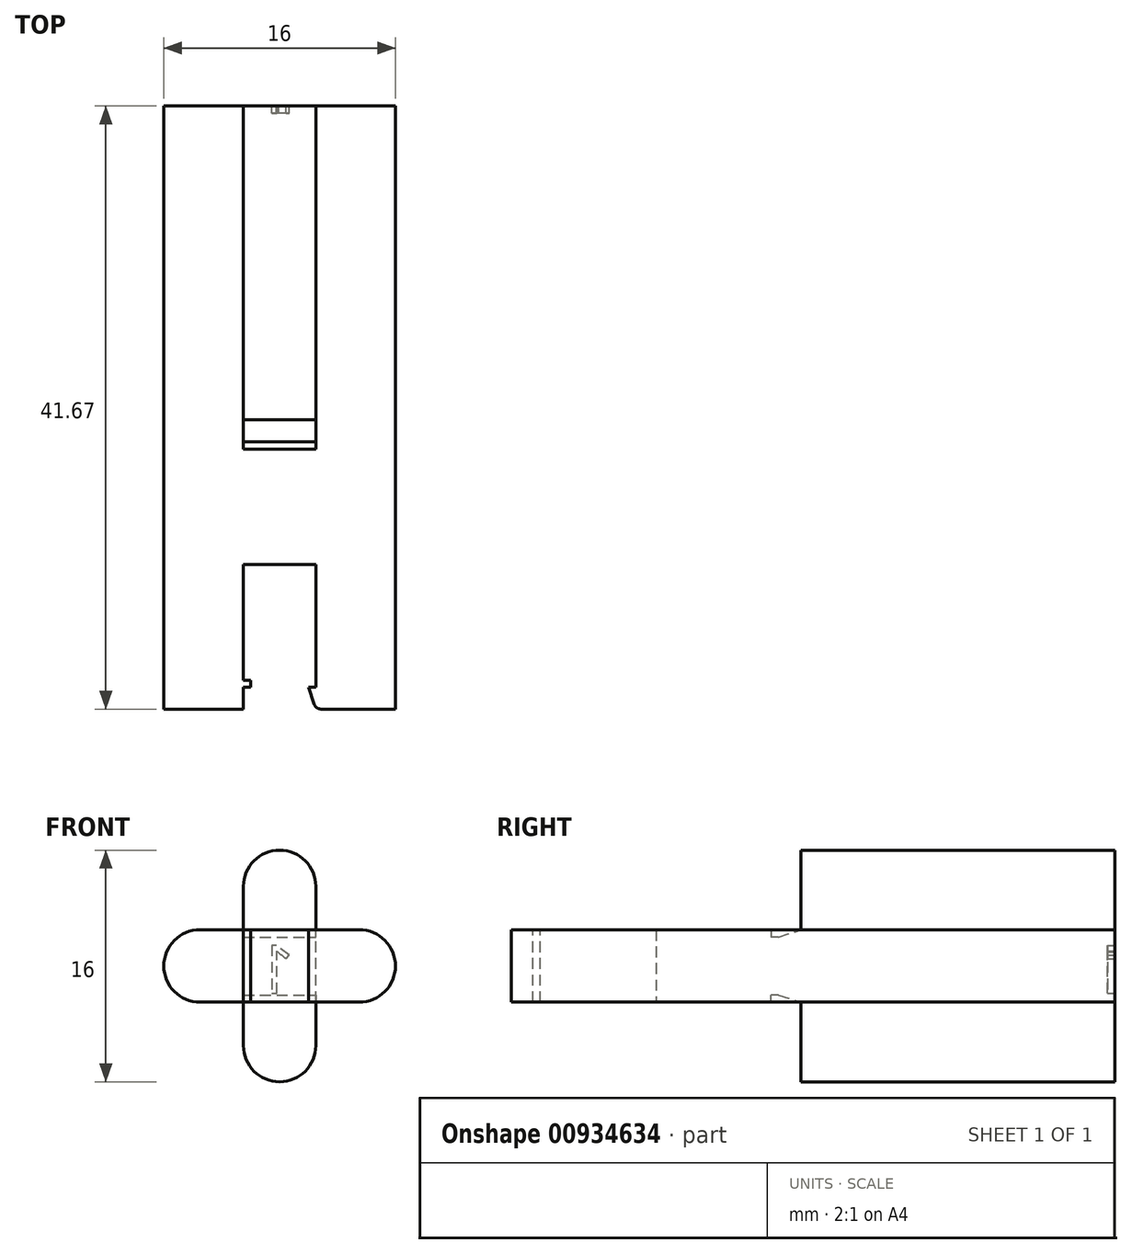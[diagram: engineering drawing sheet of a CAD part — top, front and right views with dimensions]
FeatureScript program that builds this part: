
annotation { "Feature Type Name" : "Feature", "Feature Type Description" : "" }
export const myFeature = defineFeature(function(context is Context, id is Id, definition is map)
    precondition{}
    {
        {
            var Q0;
            Q0=qCreatedBy(makeId("Front.planeOp"),FACE);
            var sketch = newSketch(context, id + "F0", { "sketchPlane" : qUnion([Q0])});
            skLineSegment(sketch, "E0.bottom", {"start": v(2.5, 8) * mm, "end": v(-2.5, 8) * mm});
            skLineSegment(sketch, "E0.top", {"start": v(2.5, -8) * mm, "end": v(-2.5, -8) * mm});
            skLineSegment(sketch, "E0.left", {"start": v(2.5, 8) * mm, "end": v(2.5, -8) * mm});
            skLineSegment(sketch, "E0.right", {"start": v(-2.5, 8) * mm, "end": v(-2.5, -8) * mm});
            skPoint(sketch, "E0.middle", {"position": v(0, 0) * mm});
            skLineSegment(sketch, "E1.bottom", {"start": v(-8, -2.5) * mm, "end": v(8, -2.5) * mm});
            skLineSegment(sketch, "E1.top", {"start": v(-8, 2.5) * mm, "end": v(8, 2.5) * mm});
            skLineSegment(sketch, "E1.left", {"start": v(-8, -2.5) * mm, "end": v(-8, 2.5) * mm});
            skLineSegment(sketch, "E1.right", {"start": v(8, -2.5) * mm, "end": v(8, 2.5) * mm});
            skSolve(sketch);
        }
        {
            var Q0;
            {var subQ5=sQuery(id+"F0.wireOp",EDGE,"E1.left");Q0=makeQuery(id+"F0.imprint","IMPRINT",FACE,{"disambiguationData":[TD([[makeQuery(id+"F0.imprint","IMPRINT",EDGE,{"derivedFrom":subQ5}),-1.0]])]});}
            var Q1;
            {var subQ0=sQuery(id+"F0.wireOp",EDGE,"E1.top");var subQ1=sQuery(id+"F0.wireOp",EDGE,"E0.left");var subQ2=makeQuery(id+"F0.imprint","INTERSECT",VERTEX,{"derivedFrom":[subQ1,subQ0]});Q1=makeQuery(id+"F0.imprint","IMPRINT",FACE,{"disambiguationData":[TD([[makeQuery(id+"F0.imprint","IMPRINT",EDGE,{"disambiguationData":[TD([[subQ2,-1.0]])],"derivedFrom":subQ1}),-1.0]])]});}
            var Q2;
            {var subQ5=sQuery(id+"F0.wireOp",EDGE,"E1.right");Q2=makeQuery(id+"F0.imprint","IMPRINT",FACE,{"disambiguationData":[TD([[makeQuery(id+"F0.imprint","IMPRINT",EDGE,{"derivedFrom":subQ5}),1.0]])]});}
            var Q3;
            {var subQ0=sQuery(id+"F0.wireOp",EDGE,"E0.top");Q3=makeQuery(id+"F0.imprint","IMPRINT",FACE,{"disambiguationData":[TD([[makeQuery(id+"F0.imprint","IMPRINT",EDGE,{"derivedFrom":subQ0}),-1.0]])]});}
            var Q4;
            {var subQ0=sQuery(id+"F0.wireOp",EDGE,"E0.bottom");Q4=makeQuery(id+"F0.imprint","IMPRINT",FACE,{"disambiguationData":[TD([[makeQuery(id+"F0.imprint","IMPRINT",EDGE,{"derivedFrom":subQ0}),1.0]])]});}
            extrude(context, id + "F1", {"entities" : qUnion([Q0, Q1, Q2, Q3, Q4]), "depth" : 233.86 * mm, "offsetDistance" : 25.4 * mm});
        }
        {
            var Q0;
            Q0=makeQuery(id+"F1.opExtrude","SWEPT_EDGE",EDGE,{"disambiguationData":[OSD([sQuery(id+"F0.wireOp",EDGE,"E0.bottom"),sQuery(id+"F0.wireOp",EDGE,"E0.right")])]});
            var Q1;
            Q1=makeQuery(id+"F1.opExtrude","SWEPT_EDGE",EDGE,{"disambiguationData":[OSD([sQuery(id+"F0.wireOp",EDGE,"E0.bottom"),sQuery(id+"F0.wireOp",EDGE,"E0.left")])]});
            var Q2;
            Q2=makeQuery(id+"F1.opExtrude","SWEPT_EDGE",EDGE,{"disambiguationData":[OSD([sQuery(id+"F0.wireOp",EDGE,"E1.top"),sQuery(id+"F0.wireOp",EDGE,"E1.left")])]});
            var Q3;
            Q3=makeQuery(id+"F1.opExtrude","SWEPT_EDGE",EDGE,{"disambiguationData":[OSD([sQuery(id+"F0.wireOp",EDGE,"E1.bottom"),sQuery(id+"F0.wireOp",EDGE,"E1.left")])]});
            var Q4;
            Q4=makeQuery(id+"F1.opExtrude","SWEPT_EDGE",EDGE,{"disambiguationData":[OSD([sQuery(id+"F0.wireOp",EDGE,"E0.top"),sQuery(id+"F0.wireOp",EDGE,"E0.right")])]});
            var Q5;
            Q5=makeQuery(id+"F1.opExtrude","SWEPT_EDGE",EDGE,{"disambiguationData":[OSD([sQuery(id+"F0.wireOp",EDGE,"E0.top"),sQuery(id+"F0.wireOp",EDGE,"E0.left")])]});
            var Q6;
            Q6=makeQuery(id+"F1.opExtrude","SWEPT_EDGE",EDGE,{"disambiguationData":[OSD([sQuery(id+"F0.wireOp",EDGE,"E1.bottom"),sQuery(id+"F0.wireOp",EDGE,"E1.right")])]});
            var Q7;
            Q7=makeQuery(id+"F1.opExtrude","SWEPT_EDGE",EDGE,{"disambiguationData":[OSD([sQuery(id+"F0.wireOp",EDGE,"E1.top"),sQuery(id+"F0.wireOp",EDGE,"E1.right")])]});
            fillet(context, id + "F2", {"entities" : qUnion([Q0, Q1, Q2, Q3, Q4, Q5, Q6, Q7]), "radius" : 2.5 * mm, "tangentPropagation" : true, "allowEdgeOverflow" : false});
        }
        {
            var Q0;
            Q0=qCreatedBy(makeId("Front.planeOp"),FACE);
            var sketch = newSketch(context, id + "F3", { "sketchPlane" : qUnion([Q0])});
            skCircle(sketch, "E2", {"center": v(0, 0) * mm, "radius": 14.75 * mm});
            skCircle(sketch, "E3", {"center": v(0, 0) * mm, "radius": 12.2 * mm});
            skSolve(sketch);
        }
        {
            var Q0;
            Q0=makeQuery(id+"F3.imprint","IMPRINT",FACE,{"disambiguationData":[TD([[makeQuery(id+"F3.imprint","IMPRINT",EDGE,{"derivedFrom":sQuery(id+"F3.wireOp",EDGE,"E2")}),1.0]])]});
            var Q1;
            Q1=makeQuery(id+"F3.imprint","IMPRINT",FACE,{"disambiguationData":[TD([[makeQuery(id+"F3.imprint","IMPRINT",EDGE,{"derivedFrom":sQuery(id+"F3.wireOp",EDGE,"E3")}),1.0]])]});
            extrude(context, id + "F4", {"entities" : qUnion([Q0, Q1]), "operationType" : NewBodyOperationType.ADD, "oppositeDirection" : true, "depth" : 13.8 * mm, "offsetDistance" : 25.4 * mm});
        }
        {
            var Q0;
            {var subQ0=sQuery(id+"F0.wireOp",EDGE,"E0.right");Q0=makeQuery(id+"F1.opExtrude","CAP_EDGE",EDGE,{"disambiguationData":[OSD([subQ0]),TDD([makeQuery(id+"F0.imprint","IMPRINT",EDGE,{"disambiguationData":[TD([[makeQuery(id+"F0.imprint","INTERSECT",VERTEX,{"derivedFrom":[sQuery(id+"F0.wireOp",EDGE,"E0.bottom"),subQ0]}),-1.0]])],"derivedFrom":subQ0})])],"isStart":true});}
            var Q1;
            Q1=makeQuery(id+"F4.opExtrude","CAP_FACE",FACE,{"disambiguationData":[OSD([sQuery(id+"F3.wireOp",EDGE,"E2")])],"isStart":true});
            var Q2;
            Q2=makeQuery(id+"F4.opExtrude","CAP_EDGE",EDGE,{"disambiguationData":[OSD([sQuery(id+"F3.wireOp",EDGE,"E2")])],"isStart":false});
            fillet(context, id + "F5", {"entities" : qUnion([Q0, Q1, Q2]), "radius" : 0.5 * mm, "tangentPropagation" : true, "allowEdgeOverflow" : false});
        }
        {
            var Q0;
            Q0=qCreatedBy(makeId("Right.planeOp"),FACE);
            var sketch = newSketch(context, id + "F6", { "sketchPlane" : qUnion([Q0])});
            skLineSegment(sketch, "E4.bottom", {"start": v(5, 22.2) * mm, "end": v(8.8, 22.2) * mm});
            skLineSegment(sketch, "E4.top", {"start": v(5, 12.2) * mm, "end": v(8.8, 12.2) * mm});
            skLineSegment(sketch, "E4.left", {"start": v(5, 22.2) * mm, "end": v(5, 12.2) * mm});
            skLineSegment(sketch, "E4.right", {"start": v(8.8, 22.2) * mm, "end": v(8.8, 12.2) * mm});
            skLineSegment(sketch, "E5", {"start": v(0, 0) * mm, "end": v(33.95, 0) * mm});
            skSolve(sketch);
        }
        {
            var Q0;
            Q0=makeQuery(id+"F6.imprint","IMPRINT",FACE,{"disambiguationData":[TD([[makeQuery(id+"F6.imprint","IMPRINT",EDGE,{"derivedFrom":sQuery(id+"F6.wireOp",EDGE,"E4.bottom")}),-1.0]])]});
            var Q1;
            Q1=sQuery(id+"F6.wireOp",EDGE,"E5");
            revolve(context, id + "F7", {"operationType" : NewBodyOperationType.REMOVE, "surfaceOperationType" : NewSurfaceOperationType.NEW, "entities" : qUnion([Q0]), "axis" : qUnion([Q1]), "revolveType" : RevolveType.FULL, "oppositeDirection" : true});
        }
        {
            var Q0;
            Q0=makeQuery(id+"F1.opExtrude","CAP_FACE",FACE,{"disambiguationData":[OSD([sQuery(id+"F0.wireOp",EDGE,"E0.bottom"),sQuery(id+"F0.wireOp",EDGE,"E0.top"),sQuery(id+"F0.wireOp",EDGE,"E0.left"),sQuery(id+"F0.wireOp",EDGE,"E0.right"),sQuery(id+"F0.wireOp",EDGE,"E1.bottom"),sQuery(id+"F0.wireOp",EDGE,"E1.top"),sQuery(id+"F0.wireOp",EDGE,"E1.left"),sQuery(id+"F0.wireOp",EDGE,"E1.right")])],"isStart":false});
            var sketch = newSketch(context, id + "F8", { "sketchPlane" : qUnion([Q0])});
            skLineSegment(sketch, "E6.bottom", {"start": v(2.5, 10) * mm, "end": v(-2.5, 10) * mm});
            skLineSegment(sketch, "E6.top", {"start": v(2.5, -10) * mm, "end": v(-2.5, -10) * mm});
            skLineSegment(sketch, "E6.left", {"start": v(2.5, 10) * mm, "end": v(2.5, -10) * mm});
            skLineSegment(sketch, "E6.right", {"start": v(-2.5, 10) * mm, "end": v(-2.5, -10) * mm});
            skPoint(sketch, "E6.middle", {"position": v(0, 0) * mm});
            skSolve(sketch);
        }
        {
            var Q0;
            {var subQ1=sQuery(id+"F0.wireOp",EDGE,"E1.top");var subQ2=sQuery(id+"F0.wireOp",EDGE,"E1.bottom");var subQ3=sQuery(id+"F0.wireOp",EDGE,"E0.right");var subQ4=sQuery(id+"F0.wireOp",EDGE,"E0.left");var subQ5=sQuery(id+"F0.wireOp",EDGE,"E0.top");var subQ6=sQuery(id+"F0.wireOp",EDGE,"E0.bottom");var subQ7=makeQuery(id+"F1.opExtrude","CAP_FACE",FACE,{"disambiguationData":[OSD([subQ6,subQ5,subQ4,subQ3,subQ2,subQ1,sQuery(id+"F0.wireOp",EDGE,"E1.left"),sQuery(id+"F0.wireOp",EDGE,"E1.right")])],"isStart":false});var subQ11=makeQuery(id+"F2.opFillet","BLEND_EDGE",EDGE,{"blendedFrom":[makeQuery(id+"F1.opExtrude","SWEPT_EDGE",EDGE,{"disambiguationData":[OSD([subQ6,subQ4])]}),subQ7],"blendedInto":[subQ7]});Q0=makeQuery(id+"F8.imprint","IMPRINT",FACE,{"disambiguationData":[TD([[makeQuery(id+"F8.imprint","IMPRINT",EDGE,{"derivedFrom":subQ11}),1.0]])]});}
            extrude(context, id + "F9", {"entities" : qUnion([Q0]), "operationType" : NewBodyOperationType.REMOVE, "oppositeDirection" : true, "depth" : 10 * mm, "offsetDistance" : 25 * mm});
        }
        {
            var Q0;
            Q0=makeQuery(id+"F9.boolean.opBoolean","COPY",FACE,{"derivedFrom":makeQuery(id+"F9.opExtrude","CAP_FACE",FACE,{"disambiguationData":[OSD([sQuery(id+"F0.wireOp",EDGE,"E0.bottom"),sQuery(id+"F0.wireOp",EDGE,"E0.top"),sQuery(id+"F0.wireOp",EDGE,"E0.left"),sQuery(id+"F0.wireOp",EDGE,"E0.right"),sQuery(id+"F0.wireOp",EDGE,"E1.bottom"),sQuery(id+"F0.wireOp",EDGE,"E1.top"),sQuery(id+"F0.wireOp",EDGE,"E1.left"),sQuery(id+"F0.wireOp",EDGE,"E1.right"),sQuery(id+"F8.wireOp",EDGE,"E6.left"),sQuery(id+"F8.wireOp",EDGE,"E6.right")])],"isStart":false})});
            var sketch = newSketch(context, id + "F10", { "sketchPlane" : qUnion([Q0])});
            skLineSegment(sketch, "E7.bottom", {"start": v(0, 8) * mm, "end": v(2.5, 8) * mm});
            skLineSegment(sketch, "E7.top", {"start": v(0, 2.5) * mm, "end": v(2.5, 2.5) * mm});
            skLineSegment(sketch, "E7.left", {"start": v(0, 8) * mm, "end": v(0, 2.5) * mm});
            skLineSegment(sketch, "E7.right", {"start": v(2.5, 8) * mm, "end": v(2.5, 2.5) * mm});
            skLineSegment(sketch, "E8.MirrorCS", {"start": v(0, 8) * mm, "end": v(-2.5, 8) * mm});
            skLineSegment(sketch, "E9.MirrorCS", {"start": v(-2.5, 8) * mm, "end": v(-2.5, 2.5) * mm});
            skLineSegment(sketch, "E10.MirrorCS", {"start": v(0, 2.5) * mm, "end": v(-2.5, 2.5) * mm});
            skLineSegment(sketch, "E11.bottom", {"start": v(-2.5, 8) * mm, "end": v(2.5, 8) * mm});
            skLineSegment(sketch, "E11.top", {"start": v(-2.5, 2.5) * mm, "end": v(2.5, 2.5) * mm});
            skLineSegment(sketch, "E12.MirrorCS", {"start": v(-2.5, -8) * mm, "end": v(-2.5, -2.5) * mm});
            skLineSegment(sketch, "E13.MirrorCS", {"start": v(-2.5, -8) * mm, "end": v(2.5, -8) * mm});
            skLineSegment(sketch, "E14.MirrorCS", {"start": v(2.5, -8) * mm, "end": v(2.5, -2.5) * mm});
            skLineSegment(sketch, "E15.MirrorCS", {"start": v(-2.5, -2.5) * mm, "end": v(2.5, -2.5) * mm});
            skSolve(sketch);
        }
        {
            var Q0;
            {var subQ15=sQuery(id+"F10.wireOp",EDGE,"E7.left");Q0=makeQuery(id+"F10.imprint","IMPRINT",FACE,{"disambiguationData":[TD([[makeQuery(id+"F10.imprint","IMPRINT",EDGE,{"derivedFrom":subQ15}),-1.0]])]});}
            var Q1;
            {var subQ13=sQuery(id+"F10.wireOp",EDGE,"E7.left");Q1=makeQuery(id+"F10.imprint","IMPRINT",FACE,{"disambiguationData":[TD([[makeQuery(id+"F10.imprint","IMPRINT",EDGE,{"derivedFrom":subQ13}),1.0]])]});}
            var Q2;
            {var subQ16=sQuery(id+"F10.wireOp",EDGE,"E15.MirrorCS");Q2=makeQuery(id+"F10.imprint","IMPRINT",FACE,{"disambiguationData":[TD([[makeQuery(id+"F10.imprint","IMPRINT",EDGE,{"derivedFrom":subQ16}),-1.0]])]});}
            extrude(context, id + "F11", {"entities" : qUnion([Q0, Q1, Q2]), "operationType" : NewBodyOperationType.REMOVE, "oppositeDirection" : true, "depth" : 10 * mm, "offsetDistance" : 25 * mm});
        }
        {
            var Q0;
            {var subQ0=sQuery(id+"F0.wireOp",EDGE,"E1.top");Q0=makeQuery(id+"F11.boolean.opBoolean","MERGE",FACE,{"derivedFrom":[makeQuery(id+"F1.opExtrude","SWEPT_FACE",FACE,{"disambiguationData":[OSD([subQ0]),TDD([makeQuery(id+"F0.imprint","IMPRINT",EDGE,{"disambiguationData":[TD([[makeQuery(id+"F0.imprint","INTERSECT",VERTEX,{"derivedFrom":[subQ0,sQuery(id+"F0.wireOp",EDGE,"E1.left")]}),-1.0]])],"derivedFrom":subQ0})])]}),makeQuery(id+"F1.opExtrude","SWEPT_FACE",FACE,{"disambiguationData":[OSD([subQ0]),TDD([makeQuery(id+"F0.imprint","IMPRINT",EDGE,{"disambiguationData":[TD([[makeQuery(id+"F0.imprint","INTERSECT",VERTEX,{"derivedFrom":[subQ0,sQuery(id+"F0.wireOp",EDGE,"E1.right")]}),1.0]])],"derivedFrom":subQ0})])]})],"fromTools":[makeQuery(id+"F11.opExtrude","SWEPT_FACE",FACE,{"disambiguationData":[OSD([sQuery(id+"F10.wireOp",EDGE,"E11.top")])]})]});}
            var sketch = newSketch(context, id + "F12", { "sketchPlane" : qUnion([Q0])});
            skLineSegment(sketch, "E16", {"start": v(2.5, -233.86) * mm, "end": v(2, -232.36) * mm});
            skLineSegment(sketch, "E17", {"start": v(2, -232.36) * mm, "end": v(2.5, -232.36) * mm});
            skLineSegment(sketch, "E18.bottom", {"start": v(2.5, -232.36) * mm, "end": v(2, -232.36) * mm});
            skLineSegment(sketch, "E18.top", {"start": v(2.5, -231.86) * mm, "end": v(2, -231.86) * mm});
            skLineSegment(sketch, "E18.left", {"start": v(2.5, -232.36) * mm, "end": v(2.5, -231.86) * mm});
            skLineSegment(sketch, "E18.right", {"start": v(2, -232.36) * mm, "end": v(2, -231.86) * mm});
            skLineSegment(sketch, "E19.bottom", {"start": v(-2.5, -233.86) * mm, "end": v(2.5, -233.86) * mm, "construction": true});
            skLineSegment(sketch, "E19.top", {"start": v(-2.5, -221.37) * mm, "end": v(2.5, -221.37) * mm, "construction": true});
            skLineSegment(sketch, "E19.left", {"start": v(-2.5, -233.86) * mm, "end": v(-2.5, -221.37) * mm, "construction": true});
            skLineSegment(sketch, "E19.right", {"start": v(2.5, -233.86) * mm, "end": v(2.5, -221.37) * mm, "construction": true});
            skLineSegment(sketch, "E20", {"start": v(0, -224.68) * mm, "end": v(0, -221.37) * mm, "construction": true});
            skPoint(sketch, "E20.startSnap0", {"position": v(0, -221.37) * mm});
            skLineSegment(sketch, "E21.MirrorCS", {"start": v(-2, -232.36) * mm, "end": v(-2.5, -232.36) * mm});
            skLineSegment(sketch, "E22.MirrorCS", {"start": v(-2.5, -232.36) * mm, "end": v(-2.5, -231.86) * mm});
            skLineSegment(sketch, "E23.MirrorCS", {"start": v(-2.5, -232.36) * mm, "end": v(-2, -232.36) * mm});
            skLineSegment(sketch, "E24.MirrorCS", {"start": v(-2, -232.36) * mm, "end": v(-2, -231.86) * mm});
            skLineSegment(sketch, "E25.MirrorCS", {"start": v(-2.5, -233.86) * mm, "end": v(-2, -232.36) * mm});
            skLineSegment(sketch, "E26.MirrorCS", {"start": v(-2.5, -231.86) * mm, "end": v(-2, -231.86) * mm});
            skSolve(sketch);
        }
        {
            var Q0;
            Q0=makeQuery(id+"F12.imprint","IMPRINT",FACE,{"disambiguationData":[TD([[makeQuery(id+"F12.imprint","IMPRINT",EDGE,{"derivedFrom":sQuery(id+"F12.wireOp",EDGE,"E22.MirrorCS")}),-1.0]])]});
            var Q1;
            {var subQ0=sQuery(id+"F12.wireOp",EDGE,"E23.MirrorCS");Q1=makeQuery(id+"F12.imprint","IMPRINT",FACE,{"disambiguationData":[TD([[makeQuery(id+"F12.imprint","IMPRINT",EDGE,{"derivedFrom":subQ0}),-1.0]])]});}
            var Q2;
            Q2=makeQuery(id+"F12.imprint","IMPRINT",FACE,{"disambiguationData":[TD([[makeQuery(id+"F12.imprint","IMPRINT",EDGE,{"derivedFrom":sQuery(id+"F12.wireOp",EDGE,"E18.bottom")}),-1.0]])]});
            var Q3;
            {var subQ0=sQuery(id+"F12.wireOp",EDGE,"E16");Q3=makeQuery(id+"F12.imprint","IMPRINT",FACE,{"disambiguationData":[TD([[makeQuery(id+"F12.imprint","IMPRINT",EDGE,{"derivedFrom":subQ0}),-1.0]])]});}
            extrude(context, id + "F13", {"entities" : qUnion([Q0, Q1, Q2, Q3]), "operationType" : NewBodyOperationType.ADD, "oppositeDirection" : true, "depth" : 5 * mm, "offsetDistance" : 25 * mm});
        }
        {
            var Q0;
            Q0=makeQuery(id+"F13.boolean.opBoolean","MERGE",EDGE,{"derivedFrom":[makeQuery(id+"F9.boolean.opBoolean","COPY",EDGE,{"derivedFrom":makeQuery(id+"F9.opExtrude","CAP_EDGE",EDGE,{"disambiguationData":[OSD([sQuery(id+"F8.wireOp",EDGE,"E6.right")])],"isStart":true})}),makeQuery(id+"F13.opExtrude","SWEPT_EDGE",EDGE,{"disambiguationData":[OSD([sQuery(id+"F0.wireOp",EDGE,"E0.right"),sQuery(id+"F0.wireOp",EDGE,"E1.top"),sQuery(id+"F12.wireOp",EDGE,"E25.MirrorCS")])]})]});
            var Q1;
            Q1=makeQuery(id+"F13.boolean.opBoolean","MERGE",EDGE,{"derivedFrom":[makeQuery(id+"F9.boolean.opBoolean","COPY",EDGE,{"derivedFrom":makeQuery(id+"F9.opExtrude","CAP_EDGE",EDGE,{"disambiguationData":[OSD([sQuery(id+"F8.wireOp",EDGE,"E6.left")])],"isStart":true})}),makeQuery(id+"F13.opExtrude","SWEPT_EDGE",EDGE,{"disambiguationData":[OSD([sQuery(id+"F0.wireOp",EDGE,"E0.left"),sQuery(id+"F0.wireOp",EDGE,"E1.top"),sQuery(id+"F12.wireOp",EDGE,"E16")])]})]});
            fillet(context, id + "F14", {"entities" : qUnion([Q0, Q1]), "radius" : .5 * mm, "tangentPropagation" : true, "allowEdgeOverflow" : false});
        }
        {
            var Q0;
            {var subQ0=sQuery(id+"F0.wireOp",EDGE,"E0.left");Q0=makeQuery(id+"F1.opExtrude","SWEPT_FACE",FACE,{"disambiguationData":[OSD([subQ0]),TDD([makeQuery(id+"F0.imprint","IMPRINT",EDGE,{"disambiguationData":[TD([[makeQuery(id+"F0.imprint","INTERSECT",VERTEX,{"derivedFrom":[sQuery(id+"F0.wireOp",EDGE,"E0.bottom"),subQ0]}),-1.0]])],"derivedFrom":subQ0})])]});}
            var sketch = newSketch(context, id + "F15", { "sketchPlane" : qUnion([Q0])});
            skLineSegment(sketch, "E27", {"start": v(-213.86, 2.5) * mm, "end": v(-213.86, -2.5) * mm, "construction": true});
            skPoint(sketch, "E28", {"position": v(-213.86, 0) * mm});
            skLineSegment(sketch, "E29", {"start": v(-213.86, 2.5) * mm, "end": v(-215.4, 2.5) * mm});
            skLineSegment(sketch, "E30", {"start": v(-215.4, 2.5) * mm, "end": v(-215.4, 2) * mm});
            skLineSegment(sketch, "E31", {"start": v(-215.4, 2) * mm, "end": v(-213.86, 2.5) * mm});
            skLineSegment(sketch, "E32.bottom", {"start": v(-215.4, 2.5) * mm, "end": v(-215.9, 2.5) * mm});
            skLineSegment(sketch, "E32.top", {"start": v(-215.4, 2) * mm, "end": v(-215.9, 2) * mm});
            skLineSegment(sketch, "E32.right", {"start": v(-215.9, 2.5) * mm, "end": v(-215.9, 2) * mm});
            skLineSegment(sketch, "E33", {"start": v(-208.07, 0) * mm, "end": v(-213.86, 0) * mm, "construction": true});
            skLineSegment(sketch, "E34.MirrorCS", {"start": v(-215.4, -2.5) * mm, "end": v(-215.4, -2) * mm});
            skLineSegment(sketch, "E35.MirrorCS", {"start": v(-215.9, -2.5) * mm, "end": v(-215.9, -2) * mm});
            skLineSegment(sketch, "E36.MirrorCS", {"start": v(-215.4, -2.5) * mm, "end": v(-215.9, -2.5) * mm});
            skLineSegment(sketch, "E37.MirrorCS", {"start": v(-215.4, -2) * mm, "end": v(-213.86, -2.5) * mm});
            skLineSegment(sketch, "E38.MirrorCS", {"start": v(-213.86, -2.5) * mm, "end": v(-215.4, -2.5) * mm});
            skLineSegment(sketch, "E39.MirrorCS", {"start": v(-215.4, -2) * mm, "end": v(-215.9, -2) * mm});
            skSolve(sketch);
        }
        {
            var Q0;
            Q0=qSketchRegion(id+"F15",true);
            extrude(context, id + "F16", {"entities" : qUnion([Q0]), "operationType" : NewBodyOperationType.REMOVE, "oppositeDirection" : true, "depth" : 5 * mm, "offsetDistance" : 25 * mm});
        }
        {
            var Q0;
            Q0=makeQuery(id+"F7.boolean.opBoolean","COPY",EDGE,{"derivedFrom":makeQuery(id+"F7.opRevolve","SWEPT_EDGE",EDGE,{"disambiguationData":[OSD([sQuery(id+"F6.wireOp",EDGE,"E4.top"),sQuery(id+"F6.wireOp",EDGE,"E4.right")])]})});
            var Q1;
            Q1=makeQuery(id+"F7.boolean.opBoolean","COPY",EDGE,{"derivedFrom":makeQuery(id+"F7.opRevolve","SWEPT_EDGE",EDGE,{"disambiguationData":[OSD([sQuery(id+"F6.wireOp",EDGE,"E4.top"),sQuery(id+"F6.wireOp",EDGE,"E4.left")])]})});
            fillet(context, id + "F17", {"entities" : qUnion([Q0, Q1]), "radius" : 1 * mm, "tangentPropagation" : true, "allowEdgeOverflow" : false});
        }
        {
            var Q0;
            Q0=qCreatedBy(makeId("Right.planeOp"),FACE);
            var sketch = newSketch(context, id + "F18", { "sketchPlane" : qUnion([Q0])});
            skLineSegment(sketch, "E40.bottom", {"start": v(-192.19, 36.93) * mm, "end": v(33.63, 36.93) * mm});
            skLineSegment(sketch, "E40.top", {"start": v(-192.19, -31.23) * mm, "end": v(33.63, -31.23) * mm});
            skLineSegment(sketch, "E40.left", {"start": v(-192.19, 36.93) * mm, "end": v(-192.19, -31.23) * mm});
            skLineSegment(sketch, "E40.right", {"start": v(33.63, 36.93) * mm, "end": v(33.63, -31.23) * mm});
            skSolve(sketch);
        }
        {
            var Q0;
            Q0=makeQuery(id+"F18.imprint","IMPRINT",FACE,{"disambiguationData":[TD([[makeQuery(id+"F18.imprint","IMPRINT",EDGE,{"derivedFrom":sQuery(id+"F18.wireOp",EDGE,"E40.bottom")}),-1.0]])]});
            extrude(context, id + "F19", {"entities" : qUnion([Q0]), "operationType" : NewBodyOperationType.REMOVE, "oppositeDirection" : true, "depth" : 35 * mm, "offsetDistance" : 25 * mm, "symmetric" : true});
        }
        {
            var Q0;
            Q0=makeQuery(id+"F19.boolean.opBoolean","COPY",FACE,{"derivedFrom":makeQuery(id+"F19.opExtrude","SWEPT_FACE",FACE,{"disambiguationData":[OSD([sQuery(id+"F18.wireOp",EDGE,"E40.left")])]})});
            var sketch = newSketch(context, id + "F20", { "sketchPlane" : qUnion([Q0])});
            skText(sketch, "E41", { "text": "1", "fontName": "OpenSans-Regular.ttf"});
            const initialGuessF20  = {"E41": [-0.00108, -0.0019, 1, 0, 0.00336]};
            skSetInitialGuess(sketch, initialGuessF20);
            skSolve(sketch);
        }
        {
            var Q0;
            Q0 = qSketchRegion(id + "F20", true);
            extrude(context, id + "F21", {"entities" : qUnion([Q0]), "operationType" : NewBodyOperationType.REMOVE, "oppositeDirection" : true, "depth" : .5 * mm, "offsetDistance" : 25 * mm});
        }
    });
